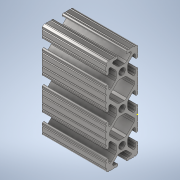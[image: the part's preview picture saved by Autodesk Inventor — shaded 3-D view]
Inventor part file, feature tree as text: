
AUTODESK INVENTOR PART (.ipt)
format: ipt  version: 2020 (Build 240168000, 168)  size: 370,688 bytes
history: native  units: in
note: dims shown in document units (in); Inventor stores cm internally (conversion verified against a paired STEP export)
features: sketch x2, extrude x1
ambient origin geometry x8: Origin, YZ Plane, XZ Plane, XY Plane, X Axis, Y Axis, Z Axis, Center Point
bodies: Solid1 (feature_tree)
feature tree (3):
  extrude  "Extrusion1"  [1 undecoded]
  sketch  "Sketch2"
  sketch  "Sketch1"  dims[d0=2.0in d1=0.0in]
note: 1 required parameter value undecoded (feature->parameter linkage not recoverable at this tier; creation-order binding heuristic only, values carry confidence <= 0.55)
